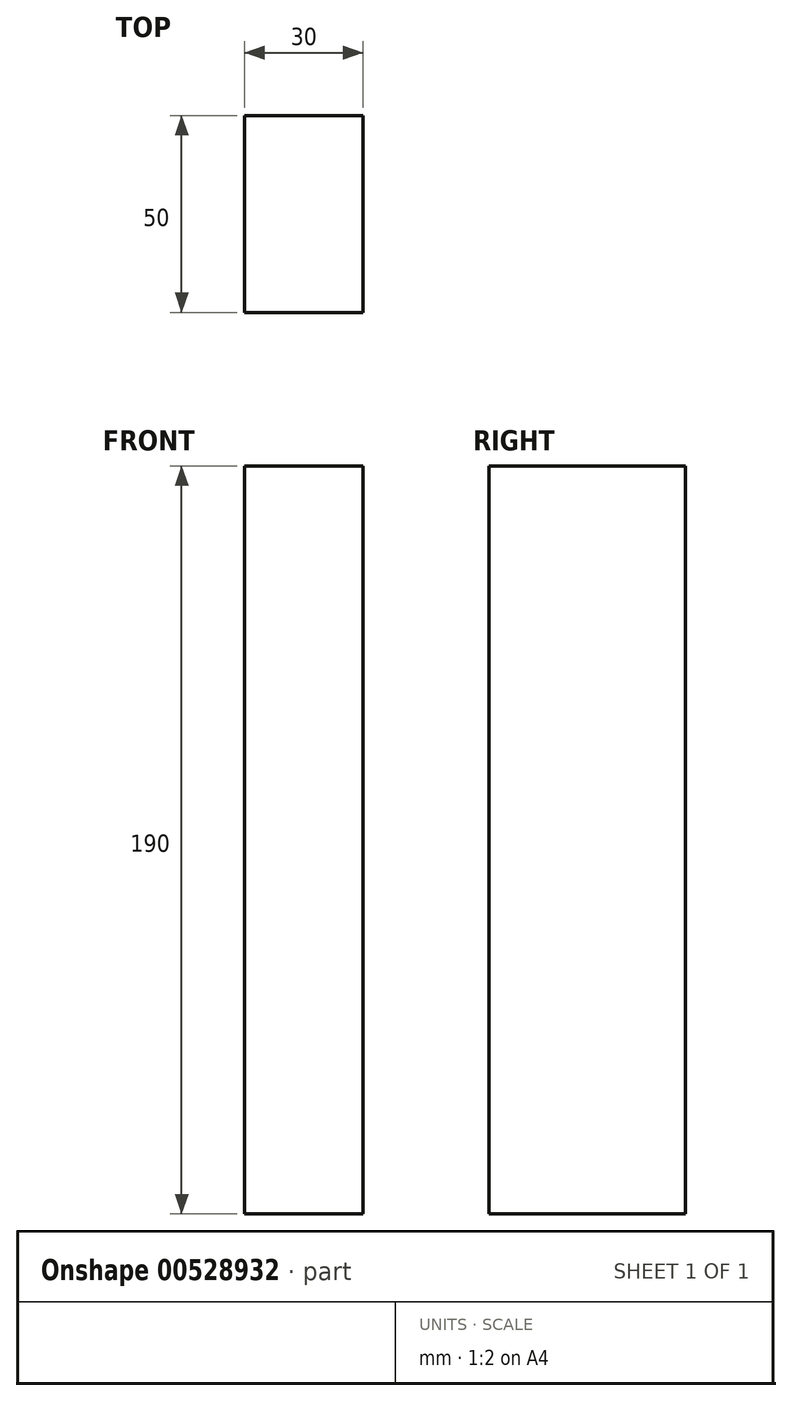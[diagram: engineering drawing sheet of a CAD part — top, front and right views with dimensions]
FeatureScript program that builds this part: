
annotation { "Feature Type Name" : "Feature", "Feature Type Description" : "" }
export const myFeature = defineFeature(function(context is Context, id is Id, definition is map)
    precondition{}
    {
        {
            var Q0;
            Q0=qCreatedBy(makeId("Top.planeOp"),FACE);
            var sketch = newSketch(context, id + "F0", { "sketchPlane" : qUnion([Q0])});
            skLineSegment(sketch, "E0.bottom", {"start": v(-15, 25) * mm, "end": v(15, 25) * mm});
            skLineSegment(sketch, "E0.top", {"start": v(-15, -25) * mm, "end": v(15, -25) * mm});
            skLineSegment(sketch, "E0.left", {"start": v(-15, 25) * mm, "end": v(-15, -25) * mm});
            skLineSegment(sketch, "E0.right", {"start": v(15, 25) * mm, "end": v(15, -25) * mm});
            skPoint(sketch, "E0.middle", {"position": v(0, 0) * mm});
            skSolve(sketch);
        }
        {
            var Q0;
            Q0 = qSketchRegion(id + "F0", true);
            extrude(context, id + "F1", {"entities" : qUnion([Q0]), "depth" : 190 * mm, "offsetDistance" : 25 * mm});
        }
    });
